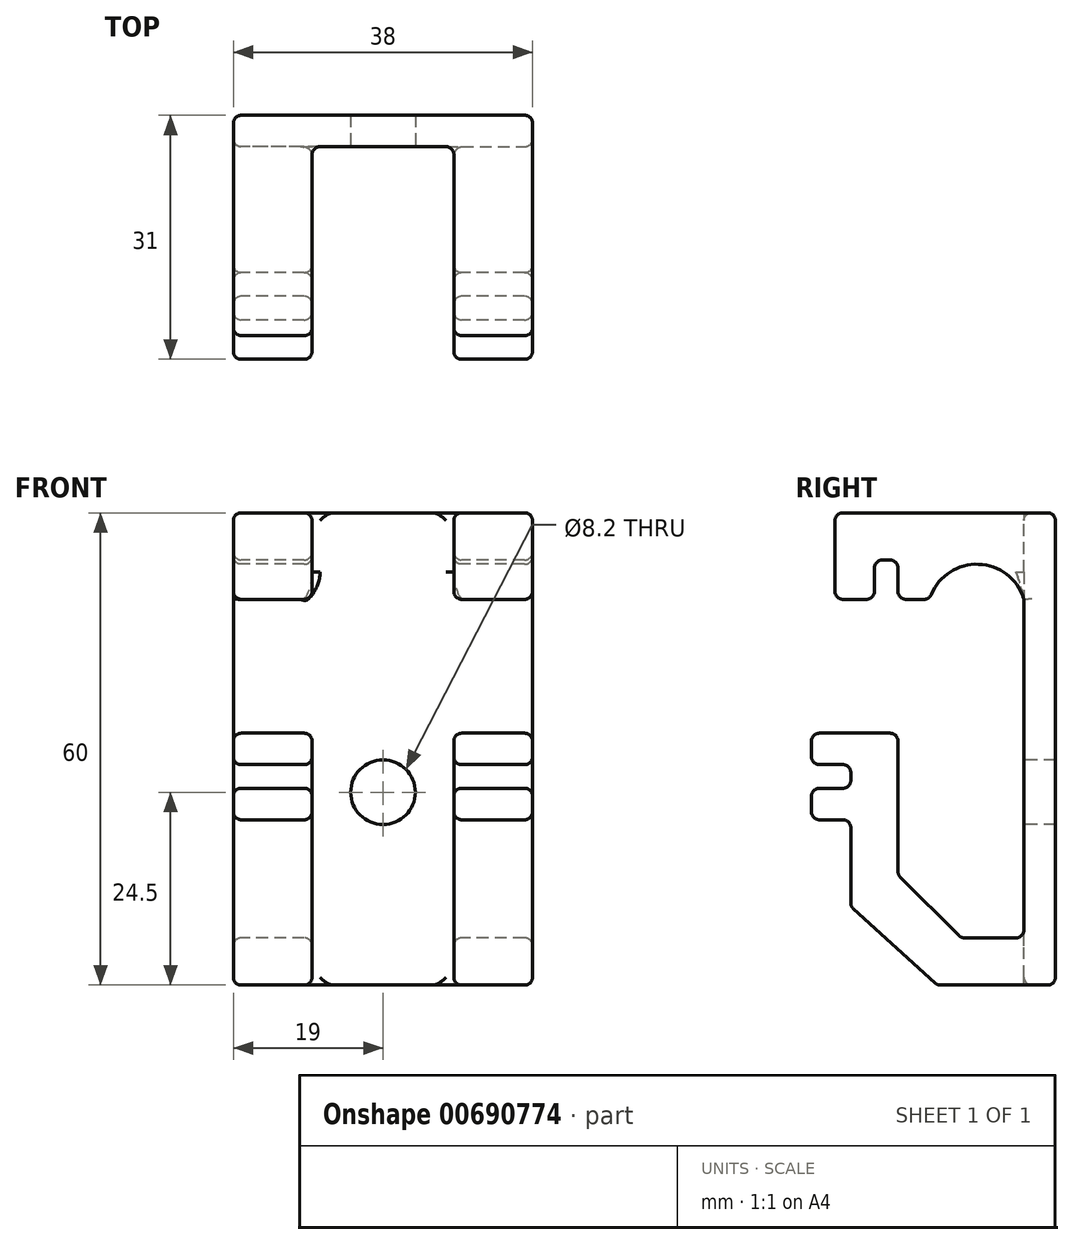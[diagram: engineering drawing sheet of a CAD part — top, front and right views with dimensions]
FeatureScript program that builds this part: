
annotation { "Feature Type Name" : "Feature", "Feature Type Description" : "" }
export const myFeature = defineFeature(function(context is Context, id is Id, definition is map)
    precondition{}
    {
        {
            var Q0;
            Q0=qCreatedBy(makeId("Right.planeOp"),FACE);
            var sketch = newSketch(context, id + "F0", { "sketchPlane" : qUnion([Q0])});
            skLineSegment(sketch, "E0", {"start": v(0, 36) * mm, "end": v(0, -24) * mm});
            skLineSegment(sketch, "E1", {"start": v(0, 36) * mm, "end": v(-28, 36) * mm});
            skLineSegment(sketch, "E2", {"start": v(-28, 36) * mm, "end": v(-28, 25) * mm});
            skLineSegment(sketch, "E3", {"start": v(-28, 25) * mm, "end": v(-23, 25) * mm});
            skLineSegment(sketch, "E4", {"start": v(-23, 25) * mm, "end": v(-23, 30) * mm});
            skLineSegment(sketch, "E5", {"start": v(-23, 30) * mm, "end": v(-20, 30) * mm});
            skLineSegment(sketch, "E6", {"start": v(-20, 30) * mm, "end": v(-20, 25) * mm});
            skLineSegment(sketch, "E7", {"start": v(-20, 25) * mm, "end": v(-16, 25) * mm});
            skLineSegment(sketch, "E8", {"start": v(-26, -3) * mm, "end": v(-31, -3) * mm});
            skLineSegment(sketch, "E9", {"start": v(-31, -3) * mm, "end": v(-31, 1) * mm});
            skLineSegment(sketch, "E10", {"start": v(-31, 1) * mm, "end": v(-26, 1) * mm});
            skLineSegment(sketch, "E11", {"start": v(-26, 1) * mm, "end": v(-26, 4) * mm});
            skLineSegment(sketch, "E12", {"start": v(-26, 4) * mm, "end": v(-31, 4) * mm});
            skLineSegment(sketch, "E13", {"start": v(-31, 4) * mm, "end": v(-31, 8) * mm});
            skLineSegment(sketch, "E14", {"start": v(-31, 8) * mm, "end": v(-20, 8) * mm});
            skLineSegment(sketch, "E15", {"start": v(-12, -18) * mm, "end": v(-4, -18) * mm});
            skLineSegment(sketch, "E16", {"start": v(-12, -18) * mm, "end": v(-20, -10) * mm});
            skLineSegment(sketch, "E17", {"start": v(-20, -10) * mm, "end": v(-20, 8) * mm});
            skLineSegment(sketch, "E18", {"start": v(-15, -24) * mm, "end": v(-26, -14) * mm});
            skLineSegment(sketch, "E19", {"start": v(-26, -14) * mm, "end": v(-26, -3) * mm});
            skLineSegment(sketch, "E20", {"start": v(0, -24) * mm, "end": v(-15, -24) * mm});
            skArc(sketch, "E21", {"start": v(-4, 25) * mm, "mid": v(-10, 29.46) * mm, "end": v(-16, 25) * mm});
            skLineSegment(sketch, "E22", {"start": v(-4, -18) * mm, "end": v(-4, 25) * mm});
            skSolve(sketch);
        }
        {
            var Q0;
            Q0 = qSketchRegion(id + "F0", true);
            extrude(context, id + "F1", {"entities" : qUnion([Q0]), "depth" : 38 * mm, "offsetDistance" : 25 * mm});
        }
        {
            var Q0;
            Q0=makeQuery(id+"F1.opExtrude","SWEPT_FACE",FACE,{"disambiguationData":[OSD([sQuery(id+"F0.wireOp",EDGE,"E22")])]});
            var sketch = newSketch(context, id + "F2", { "sketchPlane" : qUnion([Q0])});
            skLineSegment(sketch, "E23.bottom", {"start": v(28, -24) * mm, "end": v(10, -24) * mm});
            skLineSegment(sketch, "E23.top", {"start": v(28, 36) * mm, "end": v(10, 36) * mm});
            skLineSegment(sketch, "E23.left", {"start": v(28, -24) * mm, "end": v(28, 36) * mm});
            skLineSegment(sketch, "E23.right", {"start": v(10, -24) * mm, "end": v(10, 36) * mm});
            skPoint(sketch, "E23.middle", {"position": v(19, 6) * mm});
            skCircle(sketch, "E24", {"center": v(19, 0.5) * mm, "radius": 4.1 * mm});
            skSolve(sketch);
        }
        {
            var Q0;
            {var subQ5=sQuery(id+"F2.wireOp",EDGE,"E23.bottom");Q0=makeQuery(id+"F2.imprint","IMPRINT",FACE,{"disambiguationData":[TD([[makeQuery(id+"F2.imprint","IMPRINT",EDGE,{"derivedFrom":subQ5}),-1.0]])]});}
            var Q1;
            {var subQ1=sQuery(id+"F2.wireOp",EDGE,"E23.top");Q1=makeQuery(id+"F2.imprint","IMPRINT",FACE,{"disambiguationData":[TD([[makeQuery(id+"F2.imprint","IMPRINT",EDGE,{"derivedFrom":subQ1}),1.0]])]});}
            var Q2;
            {var subQ0=sQuery(id+"F2.wireOp",EDGE,"E24");var subQ1=sQuery(id+"F2.wireOp",EDGE,"hh5lU1E4-wOS6-Mn8C-MkEP-5nugExCXVxD0");var subQ2=makeQuery(id+"F2.imprint","INTERSECT",VERTEX,{"disambiguationData":[OD(0.0)],"derivedFrom":[subQ1,subQ0]});Q2=makeQuery(id+"F2.imprint","IMPRINT",FACE,{"disambiguationData":[TD([[makeQuery(id+"F2.imprint","IMPRINT",EDGE,{"disambiguationData":[TD([[subQ2,-1.0]])],"derivedFrom":subQ1}),-1.0]])]});}
            var Q3;
            {var subQ0=sQuery(id+"F2.wireOp",EDGE,"E24");var subQ1=sQuery(id+"F2.wireOp",EDGE,"hh5lU1E4-wOS6-Mn8C-MkEP-5nugExCXVxD0");var subQ2=makeQuery(id+"F2.imprint","INTERSECT",VERTEX,{"disambiguationData":[OD(0.0)],"derivedFrom":[subQ1,subQ0]});Q3=makeQuery(id+"F2.imprint","IMPRINT",FACE,{"disambiguationData":[TD([[makeQuery(id+"F2.imprint","IMPRINT",EDGE,{"disambiguationData":[TD([[subQ2,-1.0]])],"derivedFrom":subQ1}),1.0]])]});}
            var Q4;
            {var subQ6=sQuery(id+"F2.wireOp",EDGE,"E24");var subQ7=sQuery(id+"F2.wireOp",EDGE,"hh5lU1E4-wOS6-Mn8C-MkEP-5nugExCXVxD0");var subQ8=makeQuery(id+"F2.imprint","INTERSECT",VERTEX,{"disambiguationData":[OD(0.0)],"derivedFrom":[subQ7,subQ6]});Q4=makeQuery(id+"F2.imprint","IMPRINT",FACE,{"disambiguationData":[TD([[makeQuery(id+"F2.imprint","IMPRINT",EDGE,{"disambiguationData":[TD([[subQ8,1.0]])],"derivedFrom":subQ6}),-1.0]])]});}
            var Q5;
            {var subQ0=sQuery(id+"F2.wireOp",EDGE,"E24");var subQ1=sQuery(id+"F2.wireOp",EDGE,"hh5lU1E4-wOS6-Mn8C-MkEP-5nugExCXVxD0");var subQ2=makeQuery(id+"F2.imprint","INTERSECT",VERTEX,{"disambiguationData":[OD(0.0)],"derivedFrom":[subQ1,subQ0]});Q5=makeQuery(id+"F2.imprint","IMPRINT",FACE,{"disambiguationData":[TD([[makeQuery(id+"F2.imprint","IMPRINT",EDGE,{"disambiguationData":[TD([[subQ2,-1.0]])],"derivedFrom":subQ0}),-1.0]])]});}
            extrude(context, id + "F3", {"entities" : qUnion([Q0, Q1, Q2, Q3, Q4, Q5]), "operationType" : NewBodyOperationType.REMOVE, "oppositeDirection" : true, "depth" : -35 * mm, "offsetDistance" : 25 * mm});
        }
        {
            var Q0;
            Q0=makeQuery(id+"F3.boolean.opBoolean","SPLIT",FACE,{"disambiguationData":[TD([makeQuery(id+"F3.opExtrude","SWEPT_FACE",FACE,{"disambiguationData":[OSD([sQuery(id+"F2.wireOp",EDGE,"E24")])]})])],"derivedFrom":makeQuery(id+"F1.opExtrude","SWEPT_FACE",FACE,{"disambiguationData":[OSD([sQuery(id+"F0.wireOp",EDGE,"E9")])]})});
            var Q1;
            Q1=makeQuery(id+"F3.boolean.opBoolean","SPLIT",FACE,{"disambiguationData":[TD([makeQuery(id+"F3.opExtrude","SWEPT_FACE",FACE,{"disambiguationData":[OSD([sQuery(id+"F2.wireOp",EDGE,"E24")])]})])],"derivedFrom":makeQuery(id+"F1.opExtrude","SWEPT_FACE",FACE,{"disambiguationData":[OSD([sQuery(id+"F0.wireOp",EDGE,"E11")])]})});
            var Q2;
            Q2=makeQuery(id+"F3.boolean.opBoolean","SPLIT",FACE,{"disambiguationData":[TD([makeQuery(id+"F3.opExtrude","SWEPT_FACE",FACE,{"disambiguationData":[OSD([sQuery(id+"F2.wireOp",EDGE,"E24")])]})])],"derivedFrom":makeQuery(id+"F1.opExtrude","SWEPT_FACE",FACE,{"disambiguationData":[OSD([sQuery(id+"F0.wireOp",EDGE,"E13")])]})});
            var Q3;
            Q3=makeQuery(id+"F3.boolean.opBoolean","SPLIT",FACE,{"disambiguationData":[TD([makeQuery(id+"F3.opExtrude","SWEPT_FACE",FACE,{"disambiguationData":[OSD([sQuery(id+"F2.wireOp",EDGE,"E24")])]})])],"derivedFrom":makeQuery(id+"F1.opExtrude","SWEPT_FACE",FACE,{"disambiguationData":[OSD([sQuery(id+"F0.wireOp",EDGE,"E19")])]})});
            extrude(context, id + "F4", {"entities" : qUnion([Q0, Q1, Q2, Q3]), "operationType" : NewBodyOperationType.REMOVE, "oppositeDirection" : true, "depth" : 35 * mm, "offsetDistance" : 25 * mm});
        }
        {
            var Q0;
            {var subQ0=sQuery(id+"F0.wireOp",EDGE,"E2");var subQ1=sQuery(id+"F0.wireOp",EDGE,"E1");Q0=makeQuery(id+"F3.boolean.opBoolean","SPLIT",EDGE,{"disambiguationData":[TD([makeQuery(id+"F3.opExtrude","SWEPT_FACE",FACE,{"disambiguationData":[OSD([sQuery(id+"F2.wireOp",EDGE,"E23.right")])]})])],"derivedFrom":makeQuery(id+"F1.opExtrude","SWEPT_EDGE",EDGE,{"disambiguationData":[OSD([subQ1,subQ0])]})});}
            var Q1;
            {var subQ0=sQuery(id+"F0.wireOp",EDGE,"E3");var subQ1=sQuery(id+"F0.wireOp",EDGE,"E2");Q1=makeQuery(id+"F3.boolean.opBoolean","SPLIT",EDGE,{"disambiguationData":[TD([makeQuery(id+"F3.opExtrude","SWEPT_FACE",FACE,{"disambiguationData":[OSD([sQuery(id+"F2.wireOp",EDGE,"E23.right")])]})])],"derivedFrom":makeQuery(id+"F1.opExtrude","SWEPT_EDGE",EDGE,{"disambiguationData":[OSD([subQ1,subQ0])]})});}
            var Q2;
            {var subQ0=sQuery(id+"F0.wireOp",EDGE,"E3");var subQ1=sQuery(id+"F0.wireOp",EDGE,"E2");Q2=makeQuery(id+"F3.boolean.opBoolean","SPLIT",EDGE,{"disambiguationData":[TD([makeQuery(id+"F3.opExtrude","SWEPT_FACE",FACE,{"disambiguationData":[OSD([sQuery(id+"F2.wireOp",EDGE,"E23.left")])]})])],"derivedFrom":makeQuery(id+"F1.opExtrude","SWEPT_EDGE",EDGE,{"disambiguationData":[OSD([subQ1,subQ0])]})});}
            var Q3;
            {var subQ0=sQuery(id+"F0.wireOp",EDGE,"E2");var subQ1=sQuery(id+"F0.wireOp",EDGE,"E1");Q3=makeQuery(id+"F3.boolean.opBoolean","SPLIT",EDGE,{"disambiguationData":[TD([makeQuery(id+"F3.opExtrude","SWEPT_FACE",FACE,{"disambiguationData":[OSD([sQuery(id+"F2.wireOp",EDGE,"E23.left")])]})])],"derivedFrom":makeQuery(id+"F1.opExtrude","SWEPT_EDGE",EDGE,{"disambiguationData":[OSD([subQ1,subQ0])]})});}
            var Q4;
            {var subQ0=sQuery(id+"F0.wireOp",EDGE,"E14");var subQ1=sQuery(id+"F0.wireOp",EDGE,"E13");Q4=makeQuery(id+"F3.boolean.opBoolean","SPLIT",EDGE,{"disambiguationData":[TD([makeQuery(id+"F3.opExtrude","SWEPT_FACE",FACE,{"disambiguationData":[OSD([sQuery(id+"F2.wireOp",EDGE,"E23.left")])]})])],"derivedFrom":makeQuery(id+"F1.opExtrude","SWEPT_EDGE",EDGE,{"disambiguationData":[OSD([subQ1,subQ0])]})});}
            var Q5;
            {var subQ0=sQuery(id+"F0.wireOp",EDGE,"E9");var subQ1=sQuery(id+"F0.wireOp",EDGE,"E8");Q5=makeQuery(id+"F3.boolean.opBoolean","SPLIT",EDGE,{"disambiguationData":[TD([makeQuery(id+"F3.opExtrude","SWEPT_FACE",FACE,{"disambiguationData":[OSD([sQuery(id+"F2.wireOp",EDGE,"E23.left")])]})])],"derivedFrom":makeQuery(id+"F1.opExtrude","SWEPT_EDGE",EDGE,{"disambiguationData":[OSD([subQ1,subQ0])]})});}
            var Q6;
            {var subQ0=sQuery(id+"F0.wireOp",EDGE,"E14");var subQ1=sQuery(id+"F0.wireOp",EDGE,"E13");Q6=makeQuery(id+"F3.boolean.opBoolean","SPLIT",EDGE,{"disambiguationData":[TD([makeQuery(id+"F3.opExtrude","SWEPT_FACE",FACE,{"disambiguationData":[OSD([sQuery(id+"F2.wireOp",EDGE,"E23.right")])]})])],"derivedFrom":makeQuery(id+"F1.opExtrude","SWEPT_EDGE",EDGE,{"disambiguationData":[OSD([subQ1,subQ0])]})});}
            var Q7;
            {var subQ0=sQuery(id+"F0.wireOp",EDGE,"E9");var subQ1=sQuery(id+"F0.wireOp",EDGE,"E8");Q7=makeQuery(id+"F3.boolean.opBoolean","SPLIT",EDGE,{"disambiguationData":[TD([makeQuery(id+"F3.opExtrude","SWEPT_FACE",FACE,{"disambiguationData":[OSD([sQuery(id+"F2.wireOp",EDGE,"E23.right")])]})])],"derivedFrom":makeQuery(id+"F1.opExtrude","SWEPT_EDGE",EDGE,{"disambiguationData":[OSD([subQ1,subQ0])]})});}
            var Q8;
            {var subQ0=sQuery(id+"F0.wireOp",EDGE,"E10");var subQ1=sQuery(id+"F0.wireOp",EDGE,"E9");Q8=makeQuery(id+"F3.boolean.opBoolean","SPLIT",EDGE,{"disambiguationData":[TD([makeQuery(id+"F3.opExtrude","SWEPT_FACE",FACE,{"disambiguationData":[OSD([sQuery(id+"F2.wireOp",EDGE,"E23.right")])]})])],"derivedFrom":makeQuery(id+"F1.opExtrude","SWEPT_EDGE",EDGE,{"disambiguationData":[OSD([subQ1,subQ0])]})});}
            var Q9;
            {var subQ0=sQuery(id+"F0.wireOp",EDGE,"E13");var subQ1=sQuery(id+"F0.wireOp",EDGE,"E12");Q9=makeQuery(id+"F3.boolean.opBoolean","SPLIT",EDGE,{"disambiguationData":[TD([makeQuery(id+"F3.opExtrude","SWEPT_FACE",FACE,{"disambiguationData":[OSD([sQuery(id+"F2.wireOp",EDGE,"E23.right")])]})])],"derivedFrom":makeQuery(id+"F1.opExtrude","SWEPT_EDGE",EDGE,{"disambiguationData":[OSD([subQ1,subQ0])]})});}
            var Q10;
            {var subQ0=sQuery(id+"F0.wireOp",EDGE,"E7");var subQ1=sQuery(id+"F0.wireOp",EDGE,"E6");Q10=makeQuery(id+"F3.boolean.opBoolean","SPLIT",EDGE,{"disambiguationData":[TD([makeQuery(id+"F3.opExtrude","SWEPT_FACE",FACE,{"disambiguationData":[OSD([sQuery(id+"F2.wireOp",EDGE,"E23.left")])]})])],"derivedFrom":makeQuery(id+"F1.opExtrude","SWEPT_EDGE",EDGE,{"disambiguationData":[OSD([subQ1,subQ0])]})});}
            var Q11;
            {var subQ0=sQuery(id+"F0.wireOp",EDGE,"E11");var subQ1=sQuery(id+"F0.wireOp",EDGE,"E10");Q11=makeQuery(id+"F3.boolean.opBoolean","SPLIT",EDGE,{"disambiguationData":[TD([makeQuery(id+"F3.opExtrude","SWEPT_FACE",FACE,{"disambiguationData":[OSD([sQuery(id+"F2.wireOp",EDGE,"E23.left")])]})])],"derivedFrom":makeQuery(id+"F1.opExtrude","SWEPT_EDGE",EDGE,{"disambiguationData":[OSD([subQ1,subQ0])]})});}
            var Q12;
            {var subQ0=sQuery(id+"F0.wireOp",EDGE,"E11");var subQ1=sQuery(id+"F0.wireOp",EDGE,"E10");Q12=makeQuery(id+"F3.boolean.opBoolean","SPLIT",EDGE,{"disambiguationData":[TD([makeQuery(id+"F3.opExtrude","SWEPT_FACE",FACE,{"disambiguationData":[OSD([sQuery(id+"F2.wireOp",EDGE,"E23.right")])]})])],"derivedFrom":makeQuery(id+"F1.opExtrude","SWEPT_EDGE",EDGE,{"disambiguationData":[OSD([subQ1,subQ0])]})});}
            var Q13;
            {var subQ0=sQuery(id+"F0.wireOp",EDGE,"E17");var subQ1=sQuery(id+"F0.wireOp",EDGE,"E14");Q13=makeQuery(id+"F3.boolean.opBoolean","SPLIT",EDGE,{"disambiguationData":[TD([makeQuery(id+"F3.opExtrude","SWEPT_FACE",FACE,{"disambiguationData":[OSD([sQuery(id+"F2.wireOp",EDGE,"E23.left")])]})])],"derivedFrom":makeQuery(id+"F1.opExtrude","SWEPT_EDGE",EDGE,{"disambiguationData":[OSD([subQ1,subQ0])]})});}
            var Q14;
            {var subQ0=sQuery(id+"F0.wireOp",EDGE,"E10");var subQ1=sQuery(id+"F0.wireOp",EDGE,"E9");Q14=makeQuery(id+"F3.boolean.opBoolean","SPLIT",EDGE,{"disambiguationData":[TD([makeQuery(id+"F3.opExtrude","SWEPT_FACE",FACE,{"disambiguationData":[OSD([sQuery(id+"F2.wireOp",EDGE,"E23.left")])]})])],"derivedFrom":makeQuery(id+"F1.opExtrude","SWEPT_EDGE",EDGE,{"disambiguationData":[OSD([subQ1,subQ0])]})});}
            var Q15;
            {var subQ0=sQuery(id+"F0.wireOp",EDGE,"E13");var subQ1=sQuery(id+"F0.wireOp",EDGE,"E12");Q15=makeQuery(id+"F3.boolean.opBoolean","SPLIT",EDGE,{"disambiguationData":[TD([makeQuery(id+"F3.opExtrude","SWEPT_FACE",FACE,{"disambiguationData":[OSD([sQuery(id+"F2.wireOp",EDGE,"E23.left")])]})])],"derivedFrom":makeQuery(id+"F1.opExtrude","SWEPT_EDGE",EDGE,{"disambiguationData":[OSD([subQ1,subQ0])]})});}
            var Q16;
            {var subQ0=sQuery(id+"F0.wireOp",EDGE,"CpvSiToi-X1Gv-g4La-oOLz-IgAzjBGJWCwC");var subQ1=sQuery(id+"F2.wireOp",EDGE,"E23.left");var subQ2=sQuery(id+"F0.wireOp",EDGE,"E15");Q16=makeQuery(id+"F3.boolean.opBoolean","SPLIT",EDGE,{"disambiguationData":[TD([makeQuery(id+"F3.opExtrude","SWEPT_FACE",FACE,{"disambiguationData":[OSD([subQ1])]})])],"derivedFrom":makeQuery(id+"F1.opExtrude","SWEPT_EDGE",EDGE,{"disambiguationData":[OSD([subQ2,subQ0])]})});}
            var Q17;
            {var subQ0=sQuery(id+"F0.wireOp",EDGE,"E19");var subQ1=sQuery(id+"F0.wireOp",EDGE,"E8");Q17=makeQuery(id+"F3.boolean.opBoolean","SPLIT",EDGE,{"disambiguationData":[TD([makeQuery(id+"F3.opExtrude","SWEPT_FACE",FACE,{"disambiguationData":[OSD([sQuery(id+"F2.wireOp",EDGE,"E23.left")])]})])],"derivedFrom":makeQuery(id+"F1.opExtrude","SWEPT_EDGE",EDGE,{"disambiguationData":[OSD([subQ1,subQ0])]})});}
            var Q18;
            {var subQ0=sQuery(id+"F0.wireOp",EDGE,"E19");var subQ1=sQuery(id+"F0.wireOp",EDGE,"E8");Q18=makeQuery(id+"F3.boolean.opBoolean","SPLIT",EDGE,{"disambiguationData":[TD([makeQuery(id+"F3.opExtrude","SWEPT_FACE",FACE,{"disambiguationData":[OSD([sQuery(id+"F2.wireOp",EDGE,"E23.right")])]})])],"derivedFrom":makeQuery(id+"F1.opExtrude","SWEPT_EDGE",EDGE,{"disambiguationData":[OSD([subQ1,subQ0])]})});}
            var Q19;
            {var subQ0=sQuery(id+"F0.wireOp",EDGE,"E12");var subQ1=sQuery(id+"F0.wireOp",EDGE,"E11");Q19=makeQuery(id+"F3.boolean.opBoolean","SPLIT",EDGE,{"disambiguationData":[TD([makeQuery(id+"F3.opExtrude","SWEPT_FACE",FACE,{"disambiguationData":[OSD([sQuery(id+"F2.wireOp",EDGE,"E23.right")])]})])],"derivedFrom":makeQuery(id+"F1.opExtrude","SWEPT_EDGE",EDGE,{"disambiguationData":[OSD([subQ1,subQ0])]})});}
            var Q20;
            {var subQ0=sQuery(id+"F0.wireOp",EDGE,"E12");var subQ1=sQuery(id+"F0.wireOp",EDGE,"E11");Q20=makeQuery(id+"F3.boolean.opBoolean","SPLIT",EDGE,{"disambiguationData":[TD([makeQuery(id+"F3.opExtrude","SWEPT_FACE",FACE,{"disambiguationData":[OSD([sQuery(id+"F2.wireOp",EDGE,"E23.left")])]})])],"derivedFrom":makeQuery(id+"F1.opExtrude","SWEPT_EDGE",EDGE,{"disambiguationData":[OSD([subQ1,subQ0])]})});}
            var Q21;
            {var subQ0=sQuery(id+"F0.wireOp",EDGE,"E6");var subQ1=sQuery(id+"F0.wireOp",EDGE,"E5");Q21=makeQuery(id+"F3.boolean.opBoolean","SPLIT",EDGE,{"disambiguationData":[TD([makeQuery(id+"F3.opExtrude","SWEPT_FACE",FACE,{"disambiguationData":[OSD([sQuery(id+"F2.wireOp",EDGE,"E23.right")])]})])],"derivedFrom":makeQuery(id+"F1.opExtrude","SWEPT_EDGE",EDGE,{"disambiguationData":[OSD([subQ1,subQ0])]})});}
            var Q22;
            {var subQ0=sQuery(id+"F0.wireOp",EDGE,"E4");var subQ1=sQuery(id+"F0.wireOp",EDGE,"E3");Q22=makeQuery(id+"F3.boolean.opBoolean","SPLIT",EDGE,{"disambiguationData":[TD([makeQuery(id+"F3.opExtrude","SWEPT_FACE",FACE,{"disambiguationData":[OSD([sQuery(id+"F2.wireOp",EDGE,"E23.right")])]})])],"derivedFrom":makeQuery(id+"F1.opExtrude","SWEPT_EDGE",EDGE,{"disambiguationData":[OSD([subQ1,subQ0])]})});}
            var Q23;
            {var subQ0=sQuery(id+"F0.wireOp",EDGE,"E5");var subQ1=sQuery(id+"F0.wireOp",EDGE,"E4");Q23=makeQuery(id+"F3.boolean.opBoolean","SPLIT",EDGE,{"disambiguationData":[TD([makeQuery(id+"F3.opExtrude","SWEPT_FACE",FACE,{"disambiguationData":[OSD([sQuery(id+"F2.wireOp",EDGE,"E23.right")])]})])],"derivedFrom":makeQuery(id+"F1.opExtrude","SWEPT_EDGE",EDGE,{"disambiguationData":[OSD([subQ1,subQ0])]})});}
            var Q24;
            Q24=makeQuery(id+"F1.opExtrude","SWEPT_EDGE",EDGE,{"disambiguationData":[OSD([sQuery(id+"F0.wireOp",EDGE,"E0"),sQuery(id+"F0.wireOp",EDGE,"E20")])]});
            var Q25;
            {var subQ0=sQuery(id+"F0.wireOp",EDGE,"E17");var subQ1=sQuery(id+"F0.wireOp",EDGE,"E14");Q25=makeQuery(id+"F3.boolean.opBoolean","SPLIT",EDGE,{"disambiguationData":[TD([makeQuery(id+"F3.opExtrude","SWEPT_FACE",FACE,{"disambiguationData":[OSD([sQuery(id+"F2.wireOp",EDGE,"E23.right")])]})])],"derivedFrom":makeQuery(id+"F1.opExtrude","SWEPT_EDGE",EDGE,{"disambiguationData":[OSD([subQ1,subQ0])]})});}
            var Q26;
            Q26=makeQuery(id+"F1.opExtrude","SWEPT_EDGE",EDGE,{"disambiguationData":[OSD([sQuery(id+"F0.wireOp",EDGE,"E0"),sQuery(id+"F0.wireOp",EDGE,"E1")])]});
            var Q27;
            {var subQ0=sQuery(id+"F0.wireOp",EDGE,"E19");var subQ1=sQuery(id+"F0.wireOp",EDGE,"E18");Q27=makeQuery(id+"F3.boolean.opBoolean","SPLIT",EDGE,{"disambiguationData":[TD([makeQuery(id+"F3.opExtrude","SWEPT_FACE",FACE,{"disambiguationData":[OSD([sQuery(id+"F2.wireOp",EDGE,"E23.left")])]})])],"derivedFrom":makeQuery(id+"F1.opExtrude","SWEPT_EDGE",EDGE,{"disambiguationData":[OSD([subQ1,subQ0])]})});}
            var Q28;
            {var subQ0=sQuery(id+"F0.wireOp",EDGE,"E19");var subQ1=sQuery(id+"F0.wireOp",EDGE,"E18");Q28=makeQuery(id+"F3.boolean.opBoolean","SPLIT",EDGE,{"disambiguationData":[TD([makeQuery(id+"F3.opExtrude","SWEPT_FACE",FACE,{"disambiguationData":[OSD([sQuery(id+"F2.wireOp",EDGE,"E23.right")])]})])],"derivedFrom":makeQuery(id+"F1.opExtrude","SWEPT_EDGE",EDGE,{"disambiguationData":[OSD([subQ1,subQ0])]})});}
            var Q29;
            {var subQ0=sQuery(id+"F0.wireOp",EDGE,"CpvSiToi-X1Gv-g4La-oOLz-IgAzjBGJWCwC");var subQ1=sQuery(id+"F2.wireOp",EDGE,"E23.right");var subQ2=sQuery(id+"F0.wireOp",EDGE,"E15");Q29=makeQuery(id+"F3.boolean.opBoolean","SPLIT",EDGE,{"disambiguationData":[TD([makeQuery(id+"F3.opExtrude","SWEPT_FACE",FACE,{"disambiguationData":[OSD([subQ1])]})])],"derivedFrom":makeQuery(id+"F1.opExtrude","SWEPT_EDGE",EDGE,{"disambiguationData":[OSD([subQ2,subQ0])]})});}
            var Q30;
            {var subQ0=sQuery(id+"F0.wireOp",EDGE,"E20");var subQ1=sQuery(id+"F0.wireOp",EDGE,"E18");Q30=makeQuery(id+"F3.boolean.opBoolean","SPLIT",EDGE,{"disambiguationData":[TD([makeQuery(id+"F3.opExtrude","SWEPT_FACE",FACE,{"disambiguationData":[OSD([sQuery(id+"F2.wireOp",EDGE,"E23.left")])]})])],"derivedFrom":makeQuery(id+"F1.opExtrude","SWEPT_EDGE",EDGE,{"disambiguationData":[OSD([subQ1,subQ0])]})});}
            var Q31;
            {var subQ0=sQuery(id+"F0.wireOp",EDGE,"E20");var subQ1=sQuery(id+"F0.wireOp",EDGE,"E18");Q31=makeQuery(id+"F3.boolean.opBoolean","SPLIT",EDGE,{"disambiguationData":[TD([makeQuery(id+"F3.opExtrude","SWEPT_FACE",FACE,{"disambiguationData":[OSD([sQuery(id+"F2.wireOp",EDGE,"E23.right")])]})])],"derivedFrom":makeQuery(id+"F1.opExtrude","SWEPT_EDGE",EDGE,{"disambiguationData":[OSD([subQ1,subQ0])]})});}
            var Q32;
            Q32=makeQuery(id+"F3.boolean.opBoolean","INTERSECT",EDGE,{"derivedFrom":[makeQuery(id+"F1.opExtrude","SWEPT_FACE",FACE,{"disambiguationData":[OSD([sQuery(id+"F0.wireOp",EDGE,"E20")])]}),makeQuery(id+"F3.opExtrude","CAP_FACE",FACE,{"disambiguationData":[OSD([sQuery(id+"F2.wireOp",EDGE,"E23.bottom"),sQuery(id+"F2.wireOp",EDGE,"E23.top"),sQuery(id+"F2.wireOp",EDGE,"E23.left"),sQuery(id+"F2.wireOp",EDGE,"E23.right")])],"isStart":true})]});
            var Q33;
            {var subQ0=sQuery(id+"F0.wireOp",EDGE,"XjecH2wl-ARZj-F82a-KNQV-TWYw5dFAsUag");var subQ1=sQuery(id+"F0.wireOp",EDGE,"A7EVqK6k-Rogk-KSJ6-yZob-9KVNzulJ1Bah");Q33=makeQuery(id+"F3.boolean.opBoolean","SPLIT",EDGE,{"disambiguationData":[TD([makeQuery(id+"F3.opExtrude","SWEPT_FACE",FACE,{"disambiguationData":[OSD([sQuery(id+"F2.wireOp",EDGE,"E23.right")])]})])],"derivedFrom":makeQuery(id+"F1.opExtrude","SWEPT_EDGE",EDGE,{"disambiguationData":[OSD([subQ1,subQ0])]})});}
            var Q34;
            {var subQ0=sQuery(id+"F0.wireOp",EDGE,"A7EVqK6k-Rogk-KSJ6-yZob-9KVNzulJ1Bah");var subQ1=sQuery(id+"F0.wireOp",EDGE,"E7");Q34=makeQuery(id+"F3.boolean.opBoolean","SPLIT",EDGE,{"disambiguationData":[TD([makeQuery(id+"F3.opExtrude","SWEPT_FACE",FACE,{"disambiguationData":[OSD([sQuery(id+"F2.wireOp",EDGE,"E23.right")])]})])],"derivedFrom":makeQuery(id+"F1.opExtrude","SWEPT_EDGE",EDGE,{"disambiguationData":[OSD([subQ1,subQ0])]})});}
            var Q35;
            Q35=makeQuery(id+"F3.boolean.opBoolean","INTERSECT",EDGE,{"derivedFrom":[makeQuery(id+"F1.opExtrude","SWEPT_FACE",FACE,{"disambiguationData":[OSD([sQuery(id+"F0.wireOp",EDGE,"E1")])]}),makeQuery(id+"F3.opExtrude","CAP_FACE",FACE,{"disambiguationData":[OSD([sQuery(id+"F2.wireOp",EDGE,"E23.bottom"),sQuery(id+"F2.wireOp",EDGE,"E23.top"),sQuery(id+"F2.wireOp",EDGE,"E23.left"),sQuery(id+"F2.wireOp",EDGE,"E23.right")])],"isStart":true})]});
            var Q36;
            {var subQ0=sQuery(id+"F0.wireOp",EDGE,"E16");var subQ1=sQuery(id+"F0.wireOp",EDGE,"E15");Q36=makeQuery(id+"F3.boolean.opBoolean","SPLIT",EDGE,{"disambiguationData":[TD([makeQuery(id+"F3.opExtrude","SWEPT_FACE",FACE,{"disambiguationData":[OSD([sQuery(id+"F2.wireOp",EDGE,"E23.right")])]})])],"derivedFrom":makeQuery(id+"F1.opExtrude","SWEPT_EDGE",EDGE,{"disambiguationData":[OSD([subQ1,subQ0])]})});}
            var Q37;
            {var subQ0=sQuery(id+"F0.wireOp",EDGE,"E17");var subQ1=sQuery(id+"F0.wireOp",EDGE,"E16");Q37=makeQuery(id+"F3.boolean.opBoolean","SPLIT",EDGE,{"disambiguationData":[TD([makeQuery(id+"F3.opExtrude","SWEPT_FACE",FACE,{"disambiguationData":[OSD([sQuery(id+"F2.wireOp",EDGE,"E23.right")])]})])],"derivedFrom":makeQuery(id+"F1.opExtrude","SWEPT_EDGE",EDGE,{"disambiguationData":[OSD([subQ1,subQ0])]})});}
            var Q38;
            {var subQ0=sQuery(id+"F0.wireOp",EDGE,"E17");var subQ1=sQuery(id+"F0.wireOp",EDGE,"E16");Q38=makeQuery(id+"F3.boolean.opBoolean","SPLIT",EDGE,{"disambiguationData":[TD([makeQuery(id+"F3.opExtrude","SWEPT_FACE",FACE,{"disambiguationData":[OSD([sQuery(id+"F2.wireOp",EDGE,"E23.left")])]})])],"derivedFrom":makeQuery(id+"F1.opExtrude","SWEPT_EDGE",EDGE,{"disambiguationData":[OSD([subQ1,subQ0])]})});}
            var Q39;
            {var subQ0=sQuery(id+"F0.wireOp",EDGE,"E7");var subQ1=sQuery(id+"F0.wireOp",EDGE,"E6");Q39=makeQuery(id+"F3.boolean.opBoolean","SPLIT",EDGE,{"disambiguationData":[TD([makeQuery(id+"F3.opExtrude","SWEPT_FACE",FACE,{"disambiguationData":[OSD([sQuery(id+"F2.wireOp",EDGE,"E23.right")])]})])],"derivedFrom":makeQuery(id+"F1.opExtrude","SWEPT_EDGE",EDGE,{"disambiguationData":[OSD([subQ1,subQ0])]})});}
            var Q40;
            {var subQ0=sQuery(id+"F2.wireOp",EDGE,"E23.left");var subQ1=sQuery(id+"F0.wireOp",EDGE,"CpvSiToi-X1Gv-g4La-oOLz-IgAzjBGJWCwC");var subQ2=sQuery(id+"F0.wireOp",EDGE,"XjecH2wl-ARZj-F82a-KNQV-TWYw5dFAsUag");Q40=makeQuery(id+"F3.boolean.opBoolean","SPLIT",EDGE,{"disambiguationData":[TD([makeQuery(id+"F3.opExtrude","SWEPT_FACE",FACE,{"disambiguationData":[OSD([subQ0])]})])],"derivedFrom":makeQuery(id+"F1.opExtrude","SWEPT_EDGE",EDGE,{"disambiguationData":[OSD([subQ2,subQ1])]})});}
            var Q41;
            {var subQ0=sQuery(id+"F2.wireOp",EDGE,"E23.right");var subQ1=sQuery(id+"F0.wireOp",EDGE,"CpvSiToi-X1Gv-g4La-oOLz-IgAzjBGJWCwC");var subQ2=sQuery(id+"F0.wireOp",EDGE,"XjecH2wl-ARZj-F82a-KNQV-TWYw5dFAsUag");Q41=makeQuery(id+"F3.boolean.opBoolean","SPLIT",EDGE,{"disambiguationData":[TD([makeQuery(id+"F3.opExtrude","SWEPT_FACE",FACE,{"disambiguationData":[OSD([subQ0])]})])],"derivedFrom":makeQuery(id+"F1.opExtrude","SWEPT_EDGE",EDGE,{"disambiguationData":[OSD([subQ2,subQ1])]})});}
            var Q42;
            {var subQ0=sQuery(id+"F0.wireOp",EDGE,"A7EVqK6k-Rogk-KSJ6-yZob-9KVNzulJ1Bah");var subQ1=sQuery(id+"F0.wireOp",EDGE,"E7");Q42=makeQuery(id+"F3.boolean.opBoolean","SPLIT",EDGE,{"disambiguationData":[TD([makeQuery(id+"F3.opExtrude","SWEPT_FACE",FACE,{"disambiguationData":[OSD([sQuery(id+"F2.wireOp",EDGE,"E23.left")])]})])],"derivedFrom":makeQuery(id+"F1.opExtrude","SWEPT_EDGE",EDGE,{"disambiguationData":[OSD([subQ1,subQ0])]})});}
            var Q43;
            {var subQ0=sQuery(id+"F0.wireOp",EDGE,"E4");var subQ1=sQuery(id+"F0.wireOp",EDGE,"E3");Q43=makeQuery(id+"F3.boolean.opBoolean","SPLIT",EDGE,{"disambiguationData":[TD([makeQuery(id+"F3.opExtrude","SWEPT_FACE",FACE,{"disambiguationData":[OSD([sQuery(id+"F2.wireOp",EDGE,"E23.left")])]})])],"derivedFrom":makeQuery(id+"F1.opExtrude","SWEPT_EDGE",EDGE,{"disambiguationData":[OSD([subQ1,subQ0])]})});}
            var Q44;
            {var subQ1=sQuery(id+"F0.wireOp",EDGE,"E5");Q44=makeQuery(id+"F3.boolean.opBoolean","SPLIT",FACE,{"disambiguationData":[TD([makeQuery(id+"F3.opExtrude","SWEPT_FACE",FACE,{"disambiguationData":[OSD([sQuery(id+"F2.wireOp",EDGE,"E23.left")])]})])],"derivedFrom":makeQuery(id+"F1.opExtrude","SWEPT_FACE",FACE,{"disambiguationData":[OSD([subQ1])]})});}
            var Q45;
            {var subQ0=sQuery(id+"F2.wireOp",EDGE,"E23.left");var subQ2=sQuery(id+"F0.wireOp",EDGE,"XjecH2wl-ARZj-F82a-KNQV-TWYw5dFAsUag");Q45=makeQuery(id+"F3.boolean.opBoolean","SPLIT",FACE,{"disambiguationData":[TD([makeQuery(id+"F3.opExtrude","SWEPT_FACE",FACE,{"disambiguationData":[OSD([subQ0])]})])],"derivedFrom":makeQuery(id+"F1.opExtrude","SWEPT_FACE",FACE,{"disambiguationData":[OSD([subQ2])]})});}
            var Q46;
            {var subQ1=sQuery(id+"F0.wireOp",EDGE,"E7");Q46=makeQuery(id+"F3.boolean.opBoolean","SPLIT",FACE,{"disambiguationData":[TD([makeQuery(id+"F3.opExtrude","SWEPT_FACE",FACE,{"disambiguationData":[OSD([sQuery(id+"F2.wireOp",EDGE,"E23.left")])]})])],"derivedFrom":makeQuery(id+"F1.opExtrude","SWEPT_FACE",FACE,{"disambiguationData":[OSD([subQ1])]})});}
            var Q47;
            {var subQ1=sQuery(id+"F0.wireOp",EDGE,"E3");Q47=makeQuery(id+"F3.boolean.opBoolean","SPLIT",FACE,{"disambiguationData":[TD([makeQuery(id+"F3.opExtrude","SWEPT_FACE",FACE,{"disambiguationData":[OSD([sQuery(id+"F2.wireOp",EDGE,"E23.left")])]})])],"derivedFrom":makeQuery(id+"F1.opExtrude","SWEPT_FACE",FACE,{"disambiguationData":[OSD([subQ1])]})});}
            var Q48;
            {var subQ1=sQuery(id+"F0.wireOp",EDGE,"E2");Q48=makeQuery(id+"F3.boolean.opBoolean","SPLIT",FACE,{"disambiguationData":[TD([makeQuery(id+"F3.opExtrude","SWEPT_FACE",FACE,{"disambiguationData":[OSD([sQuery(id+"F2.wireOp",EDGE,"E23.left")])]})])],"derivedFrom":makeQuery(id+"F1.opExtrude","SWEPT_FACE",FACE,{"disambiguationData":[OSD([subQ1])]})});}
            var Q49;
            {var subQ0=sQuery(id+"F2.wireOp",EDGE,"E23.right");Q49=makeQuery(id+"F3.boolean.opBoolean","COPY",FACE,{"disambiguationData":[TD([makeQuery(id+"F1.opExtrude","SWEPT_FACE",FACE,{"disambiguationData":[OSD([sQuery(id+"F0.wireOp",EDGE,"E1")])]})])],"derivedFrom":makeQuery(id+"F3.opExtrude","SWEPT_FACE",FACE,{"disambiguationData":[OSD([subQ0])]})});}
            var Q50;
            Q50=makeQuery(id+"F1.opExtrude","CAP_FACE",FACE,{"disambiguationData":[OSD([sQuery(id+"F0.wireOp",EDGE,"E0"),sQuery(id+"F0.wireOp",EDGE,"E1"),sQuery(id+"F0.wireOp",EDGE,"E2"),sQuery(id+"F0.wireOp",EDGE,"E3"),sQuery(id+"F0.wireOp",EDGE,"E4"),sQuery(id+"F0.wireOp",EDGE,"E5"),sQuery(id+"F0.wireOp",EDGE,"E6"),sQuery(id+"F0.wireOp",EDGE,"E7"),sQuery(id+"F0.wireOp",EDGE,"A7EVqK6k-Rogk-KSJ6-yZob-9KVNzulJ1Bah"),sQuery(id+"F0.wireOp",EDGE,"XjecH2wl-ARZj-F82a-KNQV-TWYw5dFAsUag"),sQuery(id+"F0.wireOp",EDGE,"E8"),sQuery(id+"F0.wireOp",EDGE,"E9"),sQuery(id+"F0.wireOp",EDGE,"E10"),sQuery(id+"F0.wireOp",EDGE,"E11"),sQuery(id+"F0.wireOp",EDGE,"E12"),sQuery(id+"F0.wireOp",EDGE,"E13"),sQuery(id+"F0.wireOp",EDGE,"E14"),sQuery(id+"F0.wireOp",EDGE,"E15"),sQuery(id+"F0.wireOp",EDGE,"CpvSiToi-X1Gv-g4La-oOLz-IgAzjBGJWCwC"),sQuery(id+"F0.wireOp",EDGE,"E16"),sQuery(id+"F0.wireOp",EDGE,"E17"),sQuery(id+"F0.wireOp",EDGE,"E18"),sQuery(id+"F0.wireOp",EDGE,"E19"),sQuery(id+"F0.wireOp",EDGE,"E20")])],"isStart":false});
            var Q51;
            {var subQ0=sQuery(id+"F2.wireOp",EDGE,"E23.right");Q51=makeQuery(id+"F3.boolean.opBoolean","COPY",FACE,{"disambiguationData":[TD([makeQuery(id+"F1.opExtrude","SWEPT_FACE",FACE,{"disambiguationData":[OSD([sQuery(id+"F0.wireOp",EDGE,"E8")])]})])],"derivedFrom":makeQuery(id+"F3.opExtrude","SWEPT_FACE",FACE,{"disambiguationData":[OSD([subQ0])]})});}
            var Q52;
            Q52=makeQuery(id+"F1.opExtrude","CAP_FACE",FACE,{"disambiguationData":[OSD([sQuery(id+"F0.wireOp",EDGE,"E0"),sQuery(id+"F0.wireOp",EDGE,"E1"),sQuery(id+"F0.wireOp",EDGE,"E2"),sQuery(id+"F0.wireOp",EDGE,"E3"),sQuery(id+"F0.wireOp",EDGE,"E4"),sQuery(id+"F0.wireOp",EDGE,"E5"),sQuery(id+"F0.wireOp",EDGE,"E6"),sQuery(id+"F0.wireOp",EDGE,"E7"),sQuery(id+"F0.wireOp",EDGE,"A7EVqK6k-Rogk-KSJ6-yZob-9KVNzulJ1Bah"),sQuery(id+"F0.wireOp",EDGE,"XjecH2wl-ARZj-F82a-KNQV-TWYw5dFAsUag"),sQuery(id+"F0.wireOp",EDGE,"E8"),sQuery(id+"F0.wireOp",EDGE,"E9"),sQuery(id+"F0.wireOp",EDGE,"E10"),sQuery(id+"F0.wireOp",EDGE,"E11"),sQuery(id+"F0.wireOp",EDGE,"E12"),sQuery(id+"F0.wireOp",EDGE,"E13"),sQuery(id+"F0.wireOp",EDGE,"E14"),sQuery(id+"F0.wireOp",EDGE,"E15"),sQuery(id+"F0.wireOp",EDGE,"CpvSiToi-X1Gv-g4La-oOLz-IgAzjBGJWCwC"),sQuery(id+"F0.wireOp",EDGE,"E16"),sQuery(id+"F0.wireOp",EDGE,"E17"),sQuery(id+"F0.wireOp",EDGE,"E18"),sQuery(id+"F0.wireOp",EDGE,"E19"),sQuery(id+"F0.wireOp",EDGE,"E20")])],"isStart":true});
            var Q53;
            {var subQ0=sQuery(id+"F2.wireOp",EDGE,"E23.left");var subQ1=sQuery(id+"F0.wireOp",EDGE,"E22");var subQ2=sQuery(id+"F0.wireOp",EDGE,"E21");Q53=makeQuery(id+"F3.boolean.opBoolean","SPLIT",EDGE,{"disambiguationData":[TD([makeQuery(id+"F3.opExtrude","SWEPT_FACE",FACE,{"disambiguationData":[OSD([subQ0])]})])],"derivedFrom":makeQuery(id+"F1.opExtrude","SWEPT_EDGE",EDGE,{"disambiguationData":[OSD([subQ2,subQ1])]})});}
            var Q54;
            {var subQ0=sQuery(id+"F2.wireOp",EDGE,"E23.left");Q54=makeQuery(id+"F3.boolean.opBoolean","COPY",FACE,{"disambiguationData":[TD([makeQuery(id+"F1.opExtrude","SWEPT_FACE",FACE,{"disambiguationData":[OSD([sQuery(id+"F0.wireOp",EDGE,"E8")])]})])],"derivedFrom":makeQuery(id+"F3.opExtrude","SWEPT_FACE",FACE,{"disambiguationData":[OSD([subQ0])]})});}
            var Q55;
            {var subQ0=sQuery(id+"F2.wireOp",EDGE,"E23.left");Q55=makeQuery(id+"F3.boolean.opBoolean","COPY",EDGE,{"disambiguationData":[TD([makeQuery(id+"F1.opExtrude","SWEPT_FACE",FACE,{"disambiguationData":[OSD([sQuery(id+"F0.wireOp",EDGE,"E1")])]})])],"derivedFrom":makeQuery(id+"F3.opExtrude","CAP_EDGE",EDGE,{"disambiguationData":[OSD([subQ0])],"isStart":true})});}
            var Q56;
            {var subQ0=sQuery(id+"F2.wireOp",EDGE,"E23.left");Q56=makeQuery(id+"F3.boolean.opBoolean","COPY",FACE,{"disambiguationData":[TD([makeQuery(id+"F1.opExtrude","SWEPT_FACE",FACE,{"disambiguationData":[OSD([sQuery(id+"F0.wireOp",EDGE,"E1")])]})])],"derivedFrom":makeQuery(id+"F3.opExtrude","SWEPT_FACE",FACE,{"disambiguationData":[OSD([subQ0])]})});}
            fillet(context, id + "F5", {"entities" : qUnion([Q0, Q1, Q2, Q3, Q4, Q5, Q6, Q7, Q8, Q9, Q10, Q11, Q12, Q13, Q14, Q15, Q16, Q17, Q18, Q19, Q20, Q21, Q22, Q23, Q24, Q25, Q26, Q27, Q28, Q29, Q30, Q31, Q32, Q33, Q34, Q35, Q36, Q37, Q38, Q39, Q40, Q41, Q42, Q43, Q44, Q45, Q46, Q47, Q48, Q49, Q50, Q51, Q52, Q53, Q54, Q55, Q56]), "radius" : 1 * mm, "tangentPropagation" : true, "allowEdgeOverflow" : false});
        }
    });
